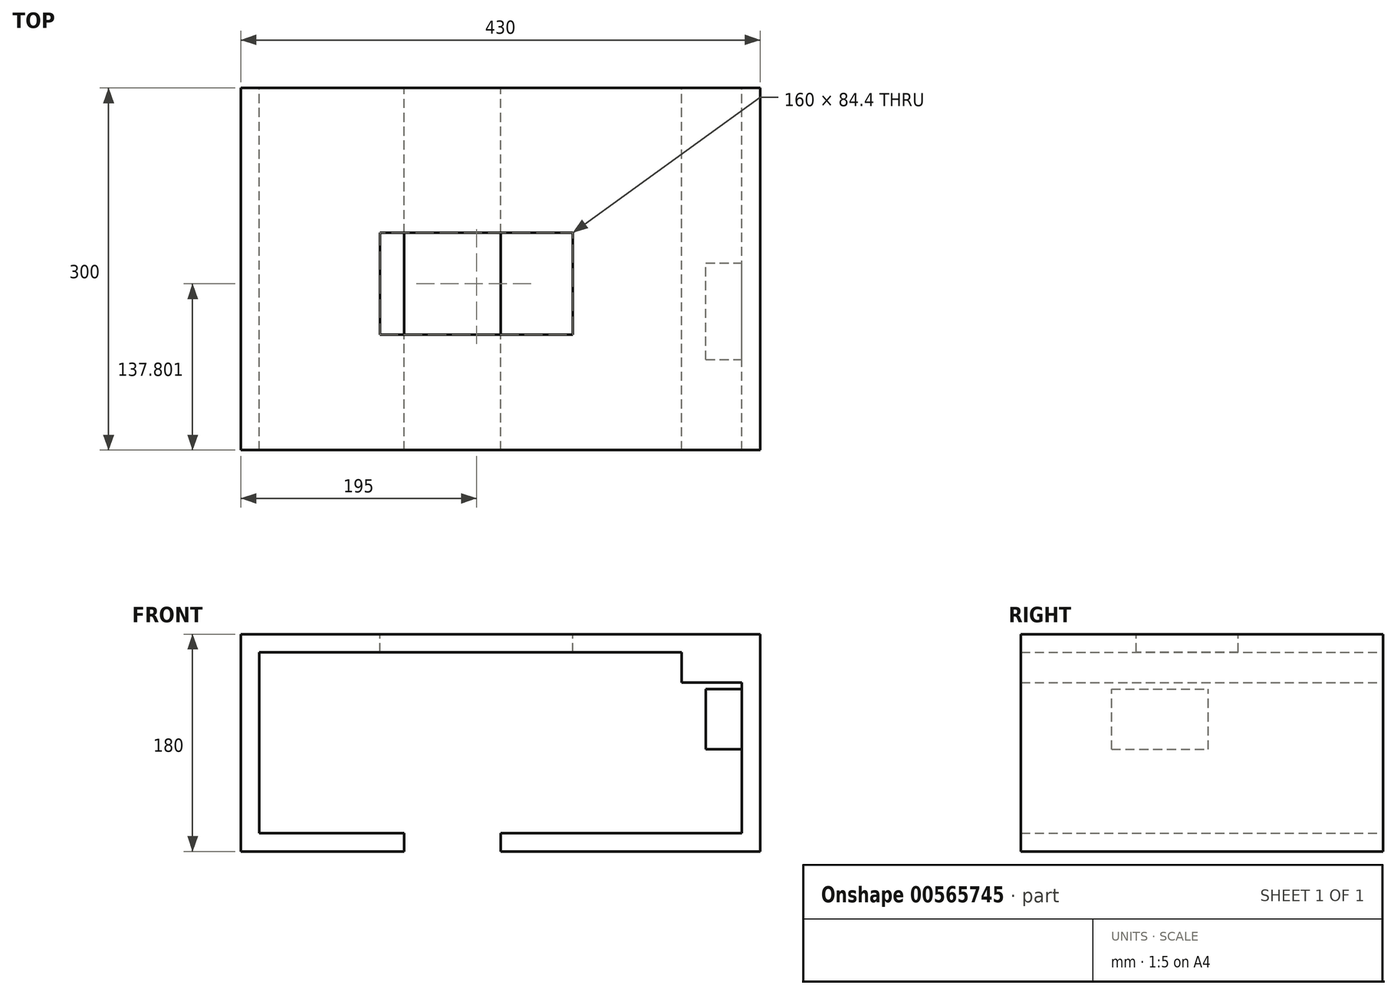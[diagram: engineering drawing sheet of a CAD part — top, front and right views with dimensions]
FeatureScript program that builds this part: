
annotation { "Feature Type Name" : "Feature", "Feature Type Description" : "" }
export const myFeature = defineFeature(function(context is Context, id is Id, definition is map)
    precondition{}
    {
        {
            var Q0;
            Q0=qCreatedBy(makeId("Front.planeOp"),FACE);
            var sketch = newSketch(context, id + "F0", { "sketchPlane" : qUnion([Q0])});
            skLineSegment(sketch, "E0", {"start": v(-80, 0) * mm, "end": v(-200, 0) * mm});
            skLineSegment(sketch, "E1", {"start": v(-200, 0) * mm, "end": v(-200, 150) * mm});
            skLineSegment(sketch, "E2", {"start": v(-200, 150) * mm, "end": v(150, 150) * mm});
            skLineSegment(sketch, "E3", {"start": v(200, 125) * mm, "end": v(200, 0) * mm});
            skLineSegment(sketch, "E4", {"start": v(200, 0) * mm, "end": v(0, 0) * mm});
            skLineSegment(sketch, "E5", {"start": v(-80, 0) * mm, "end": v(-80, -15) * mm});
            skLineSegment(sketch, "E6", {"start": v(-80, -15) * mm, "end": v(-215, -15) * mm});
            skLineSegment(sketch, "E7", {"start": v(-215, -15) * mm, "end": v(-215, 165) * mm});
            skLineSegment(sketch, "E8", {"start": v(-215, 165) * mm, "end": v(215, 165) * mm});
            skLineSegment(sketch, "E9", {"start": v(215, 165) * mm, "end": v(215, -15) * mm});
            skLineSegment(sketch, "E10", {"start": v(215, -15) * mm, "end": v(0, -15) * mm});
            skLineSegment(sketch, "E11", {"start": v(0, -15) * mm, "end": v(0, 0) * mm});
            skLineSegment(sketch, "E12", {"start": v(200, 125) * mm, "end": v(150, 125) * mm});
            skLineSegment(sketch, "E13", {"start": v(150, 125) * mm, "end": v(150, 150) * mm});
            skSolve(sketch);
        }
        {
            var Q0;
            Q0 = qSketchRegion(id + "F0", true);
            extrude(context, id + "F1", {"entities" : qUnion([Q0]), "depth" : 300 * mm, "offsetDistance" : 25 * mm});
        }
        {
            var Q0;
            Q0=makeQuery(id+"F1.opExtrude","SWEPT_FACE",FACE,{"disambiguationData":[OSD([sQuery(id+"F0.wireOp",EDGE,"E8")])]});
            var sketch = newSketch(context, id + "F2", { "sketchPlane" : qUnion([Q0])});
            skLineSegment(sketch, "E14.bottom", {"start": v(60, -120) * mm, "end": v(-100, -120) * mm});
            skLineSegment(sketch, "E14.top", {"start": v(60, -204.4) * mm, "end": v(-100, -204.4) * mm});
            skLineSegment(sketch, "E14.left", {"start": v(60, -120) * mm, "end": v(60, -204.4) * mm});
            skLineSegment(sketch, "E14.right", {"start": v(-100, -120) * mm, "end": v(-100, -204.4) * mm});
            skSolve(sketch);
        }
        {
            var Q0;
            Q0 = qSketchRegion(id + "F2", true);
            extrude(context, id + "F3", {"entities" : qUnion([Q0]), "operationType" : NewBodyOperationType.REMOVE, "oppositeDirection" : true, "depth" : 25 * mm, "offsetDistance" : 25 * mm});
        }
        {
            var Q0;
            Q0=makeQuery(id+"F1.opExtrude","SWEPT_FACE",FACE,{"disambiguationData":[OSD([sQuery(id+"F0.wireOp",EDGE,"E3")])]});
            var sketch = newSketch(context, id + "F4", { "sketchPlane" : qUnion([Q0])});
            skLineSegment(sketch, "E15.bottom", {"start": v(225, 69.53) * mm, "end": v(145, 69.53) * mm});
            skLineSegment(sketch, "E15.top", {"start": v(225, 119.53) * mm, "end": v(145, 119.53) * mm});
            skLineSegment(sketch, "E15.left", {"start": v(225, 69.53) * mm, "end": v(225, 119.53) * mm});
            skLineSegment(sketch, "E15.right", {"start": v(145, 69.53) * mm, "end": v(145, 119.53) * mm});
            skPoint(sketch, "E15.middle", {"position": v(185, 94.53) * mm});
            skSolve(sketch);
        }
        {
            var Q0;
            Q0 = qSketchRegion(id + "F4", true);
            extrude(context, id + "F5", {"entities" : qUnion([Q0]), "operationType" : NewBodyOperationType.ADD, "depth" : 30 * mm, "offsetDistance" : 25 * mm});
        }
    });
